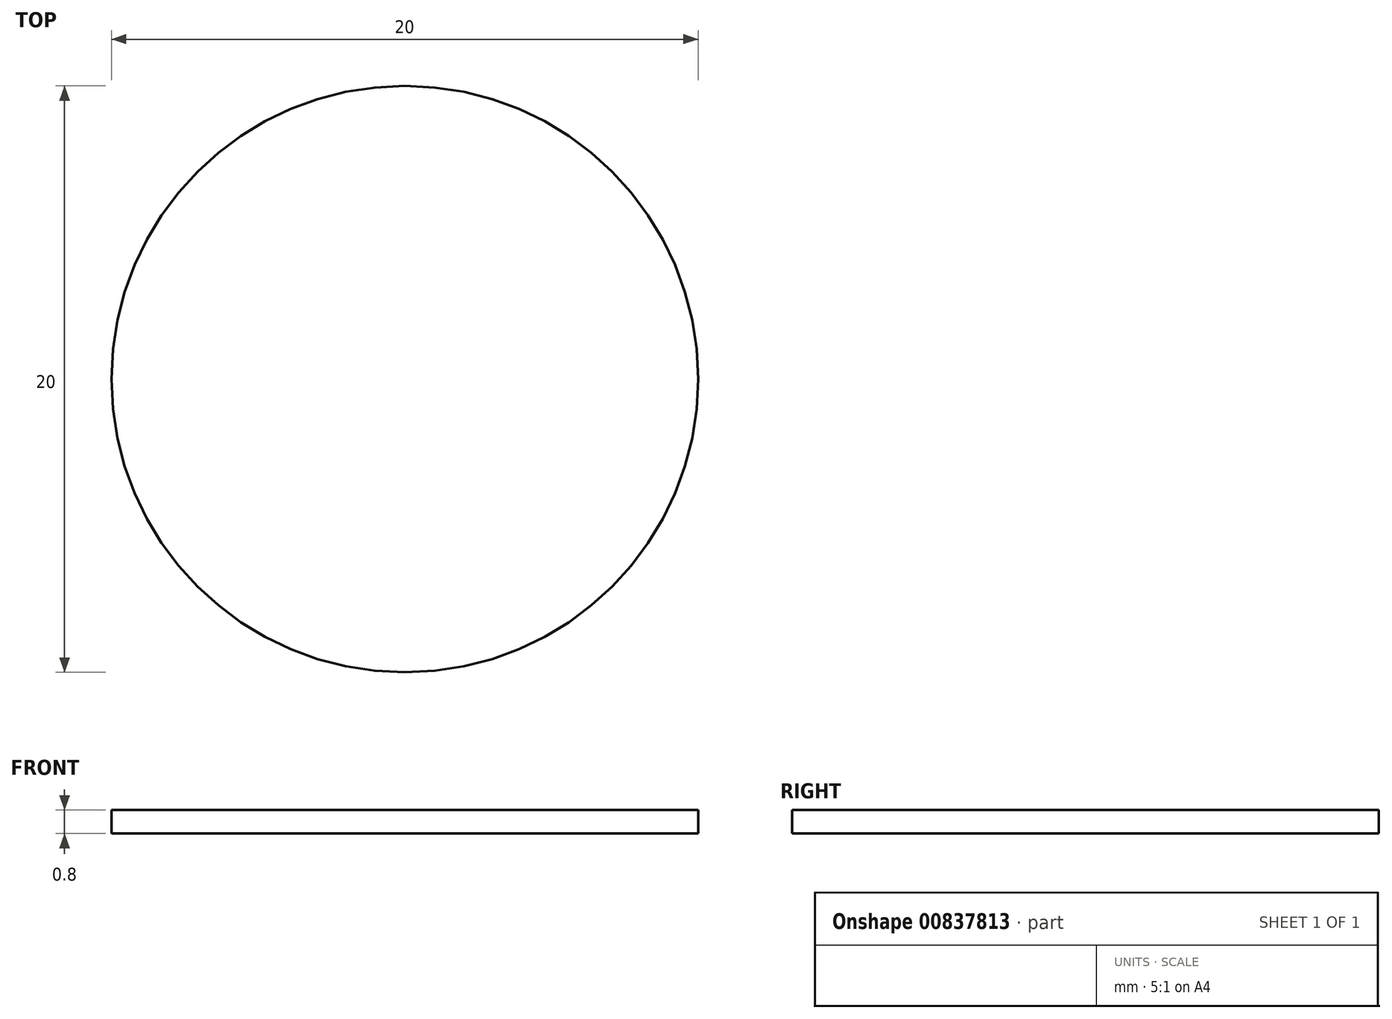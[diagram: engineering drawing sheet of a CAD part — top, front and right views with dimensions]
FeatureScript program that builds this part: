
annotation { "Feature Type Name" : "Feature", "Feature Type Description" : "" }
export const myFeature = defineFeature(function(context is Context, id is Id, definition is map)
    precondition{}
    {
        {
            var Q0;
            Q0=qCreatedBy(makeId("Top.planeOp"),FACE);
            var sketch = newSketch(context, id + "F0", { "sketchPlane" : qUnion([Q0])});
            skCircle(sketch, "E0", {"center": v(0, 0) * mm, "radius": 10 * mm});
            skSolve(sketch);
        }
        {
            var Q0;
            Q0=makeQuery(id+"F0.imprint","IMPRINT",FACE,{"disambiguationData":[TD([[makeQuery(id+"F0.imprint","IMPRINT",EDGE,{"derivedFrom":sQuery(id+"F0.wireOp",EDGE,"E0")}),1.0]])]});
            extrude(context, id + "F1", {"entities" : qUnion([Q0]), "depth" : 0.8 * mm, "offsetDistance" : 25 * mm});
        }
    });
